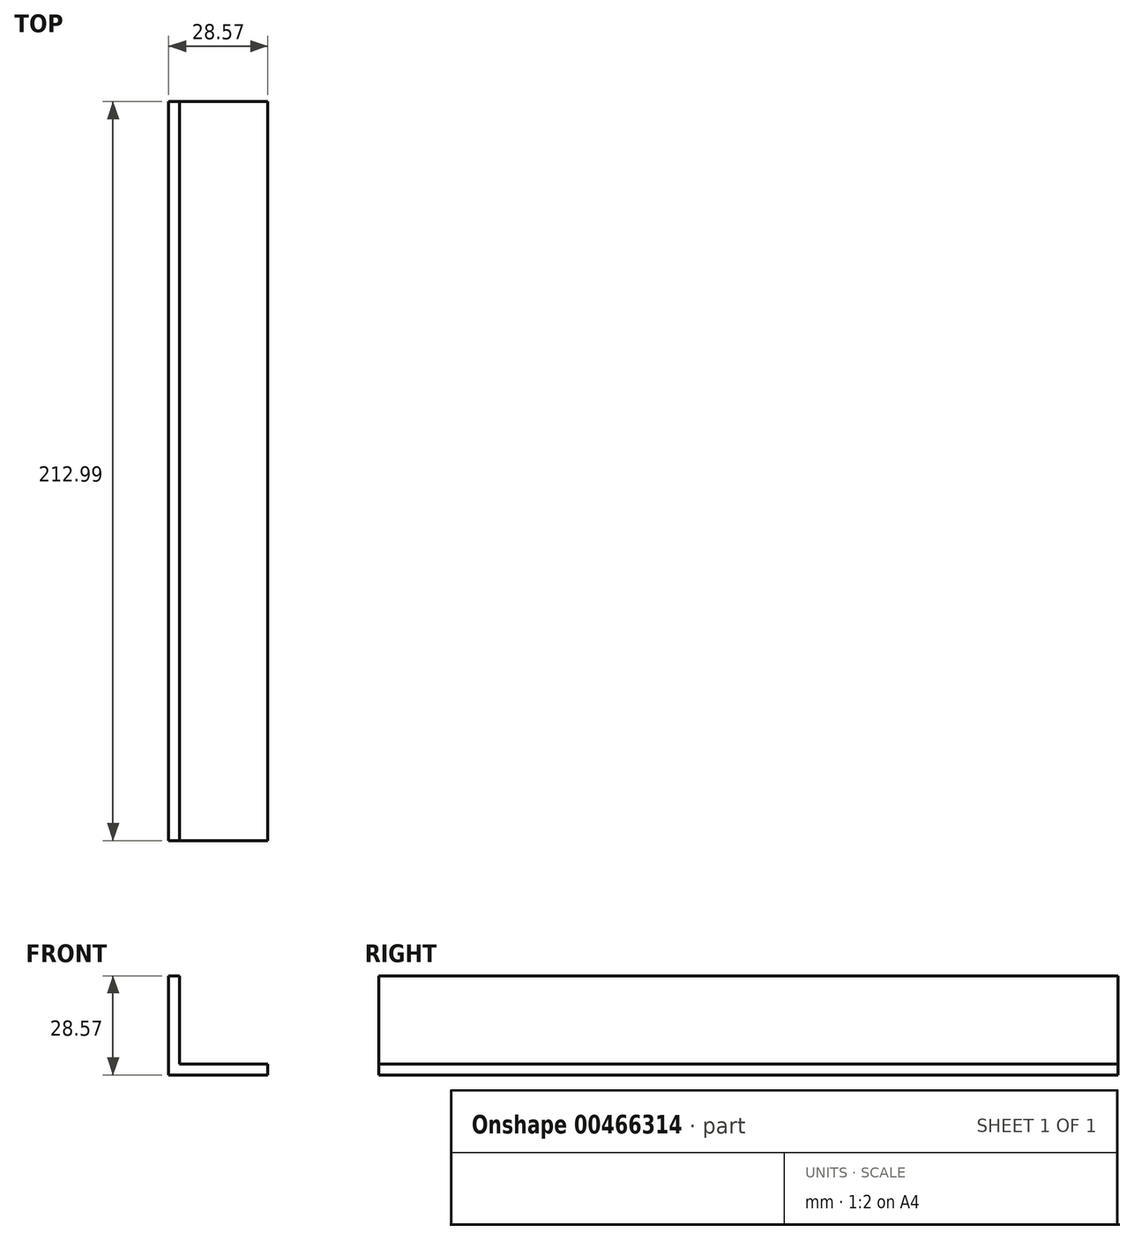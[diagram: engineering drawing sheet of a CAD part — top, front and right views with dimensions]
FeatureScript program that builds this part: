
annotation { "Feature Type Name" : "Feature", "Feature Type Description" : "" }
export const myFeature = defineFeature(function(context is Context, id is Id, definition is map)
    precondition{}
    {
        {
            var Q0;
            Q0=qCreatedBy(makeId("Front.planeOp"),FACE);
            var sketch = newSketch(context, id + "F0", { "sketchPlane" : qUnion([Q0])});
            skLineSegment(sketch, "E0", {"start": v(-25.4, -17.46) * mm, "end": v(0, -17.46) * mm});
            skLineSegment(sketch, "E1", {"start": v(-25.4, -17.46) * mm, "end": v(-25.4, 7.94) * mm});
            skLineSegment(sketch, "E2", {"start": v(-25.4, 7.94) * mm, "end": v(-28.58, 7.94) * mm});
            skLineSegment(sketch, "E3", {"start": v(-28.57, 7.94) * mm, "end": v(-28.57, -20.63) * mm});
            skLineSegment(sketch, "E4", {"start": v(0, -17.46) * mm, "end": v(0, -20.63) * mm});
            skLineSegment(sketch, "E5", {"start": v(0, -20.63) * mm, "end": v(-28.58, -20.63) * mm});
            skSolve(sketch);
        }
        {
            var Q0;
            Q0=qSketchRegion(id+"F0",true);
            extrude(context, id + "F1", {"entities" : qUnion([Q0]), "depth" : 213 * mm});
        }
    });
